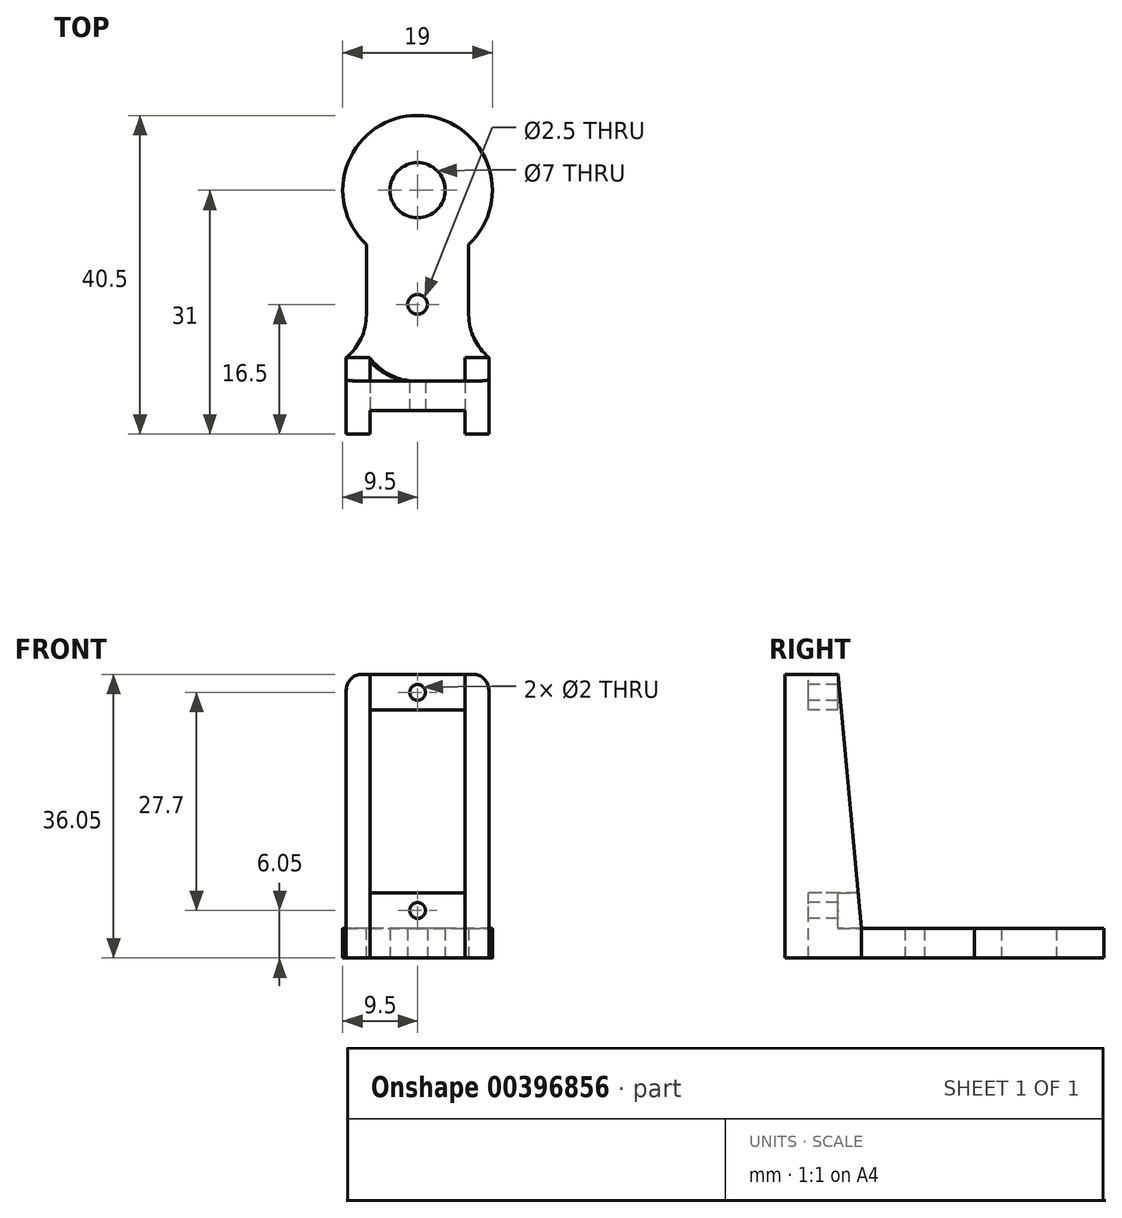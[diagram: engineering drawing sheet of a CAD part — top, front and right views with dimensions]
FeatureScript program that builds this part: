
annotation { "Feature Type Name" : "Feature", "Feature Type Description" : "" }
export const myFeature = defineFeature(function(context is Context, id is Id, definition is map)
    precondition{}
    {
        {
            var Q0;
            Q0=qCreatedBy(makeId("Top.planeOp"),FACE);
            var sketch = newSketch(context, id + "F0", { "sketchPlane" : qUnion([Q0])});
            skCircle(sketch, "E0", {"center": v(0, 0) * mm, "radius": 3.5 * mm});
            skCircle(sketch, "E1", {"center": v(0, 14.5) * mm, "radius": 1.25 * mm});
            skCircle(sketch, "E2", {"center": v(0, 0) * mm, "radius": 6.5 * mm});
            skLineSegment(sketch, "E3.bottom", {"start": v(6.5, 0) * mm, "end": v(-6.5, 0) * mm});
            skLineSegment(sketch, "E3.top", {"start": v(6.5, -28) * mm, "end": v(-6.5, -28) * mm});
            skLineSegment(sketch, "E3.left", {"start": v(6.5, -28) * mm, "end": v(6.5, 0) * mm});
            skLineSegment(sketch, "E3.right", {"start": v(-6.5, -28) * mm, "end": v(-6.5, 0) * mm});
            skCircle(sketch, "E4", {"center": v(0, 14.5) * mm, "radius": 4.25 * mm});
            skLineSegment(sketch, "E5", {"start": v(-6.42, 1) * mm, "end": v(-4.2, 15.16) * mm});
            skLineSegment(sketch, "E6", {"start": v(4.2, 15.16) * mm, "end": v(6.42, 1) * mm});
            skCircle(sketch, "E7", {"center": v(0, -14.5) * mm, "radius": 1.25 * mm});
            skCircle(sketch, "E8", {"center": v(0, 0) * mm, "radius": 9.5 * mm});
            skSolve(sketch);
        }
        {
            var Q0;
            {var subQ1=sQuery(id+"F0.wireOp",EDGE,"E3.top");Q0=makeQuery(id+"F0.imprint","IMPRINT",FACE,{"disambiguationData":[TD([[makeQuery(id+"F0.imprint","IMPRINT",EDGE,{"derivedFrom":subQ1}),-1.0]])]});}
            var Q1;
            {var subQ1=sQuery(id+"F0.wireOp",EDGE,"E2");var subQ3=sQuery(id+"F0.wireOp",EDGE,"E6");var subQ4=makeQuery(id+"F0.imprint","INTERSECT",VERTEX,{"derivedFrom":[subQ1,subQ3]});Q1=makeQuery(id+"F0.imprint","IMPRINT",FACE,{"disambiguationData":[TD([[makeQuery(id+"F0.imprint","IMPRINT",EDGE,{"disambiguationData":[TD([[subQ4,1.0]])],"derivedFrom":subQ3}),1.0]])]});}
            var Q2;
            {var subQ1=sQuery(id+"F0.wireOp",EDGE,"E2");var subQ3=sQuery(id+"F0.wireOp",EDGE,"E5");var subQ4=makeQuery(id+"F0.imprint","INTERSECT",VERTEX,{"derivedFrom":[subQ1,subQ3]});Q2=makeQuery(id+"F0.imprint","IMPRINT",FACE,{"disambiguationData":[TD([[makeQuery(id+"F0.imprint","IMPRINT",EDGE,{"disambiguationData":[TD([[subQ4,-1.0]])],"derivedFrom":subQ3}),1.0]])]});}
            var Q3;
            {var subQ0=sQuery(id+"F0.wireOp",EDGE,"E5");var subQ1=sQuery(id+"F0.wireOp",EDGE,"E2");var subQ2=makeQuery(id+"F0.imprint","INTERSECT",VERTEX,{"derivedFrom":[subQ1,subQ0]});Q3=makeQuery(id+"F0.imprint","IMPRINT",FACE,{"disambiguationData":[TD([[makeQuery(id+"F0.imprint","IMPRINT",EDGE,{"disambiguationData":[TD([[subQ2,1.0]])],"derivedFrom":subQ1}),-1.0]])]});}
            var Q4;
            {var subQ0=sQuery(id+"F0.wireOp",EDGE,"E3.left");var subQ6=sQuery(id+"F0.wireOp",EDGE,"E8");var subQ7=makeQuery(id+"F0.imprint","INTERSECT",VERTEX,{"derivedFrom":[subQ0,subQ6]});Q4=makeQuery(id+"F0.imprint","IMPRINT",FACE,{"disambiguationData":[TD([[makeQuery(id+"F0.imprint","IMPRINT",EDGE,{"disambiguationData":[TD([[subQ7,1.0]])],"derivedFrom":subQ6}),1.0]])]});}
            var Q5;
            {var subQ0=sQuery(id+"F0.wireOp",EDGE,"E3.bottom");var subQ1=sQuery(id+"F0.wireOp",EDGE,"E0");var subQ2=makeQuery(id+"F0.imprint","INTERSECT",VERTEX,{"disambiguationData":[OD(0.0)],"derivedFrom":[subQ1,subQ0]});Q5=makeQuery(id+"F0.imprint","IMPRINT",FACE,{"disambiguationData":[TD([[makeQuery(id+"F0.imprint","IMPRINT",EDGE,{"disambiguationData":[TD([[subQ2,1.0]])],"derivedFrom":subQ1}),-1.0]])]});}
            var Q6;
            {var subQ3=sQuery(id+"F0.wireOp",EDGE,"E3.bottom");var subQ6=sQuery(id+"F0.wireOp",EDGE,"E0");var subQ7=makeQuery(id+"F0.imprint","INTERSECT",VERTEX,{"disambiguationData":[OD(0.0)],"derivedFrom":[subQ6,subQ3]});Q6=makeQuery(id+"F0.imprint","IMPRINT",FACE,{"disambiguationData":[TD([[makeQuery(id+"F0.imprint","IMPRINT",EDGE,{"disambiguationData":[TD([[subQ7,-1.0]])],"derivedFrom":subQ6}),-1.0]])]});}
            extrude(context, id + "F1", {"entities" : qUnion([Q0, Q1, Q2, Q3, Q4, Q5, Q6]), "depth" : 3.75 * mm, "offsetDistance" : 25 * mm});
        }
        {
            var Q0;
            Q0=makeQuery(id+"F1.opExtrude","SWEPT_FACE",FACE,{"disambiguationData":[OSD([sQuery(id+"F0.wireOp",EDGE,"E3.top")])]});
            cPlane(context, id + "F2", {"entities" : qUnion([Q0]), "cplaneType" : CPlaneType.OFFSET, "offset" : 0 * mm, "width" : 150 * mm, "height" : 150 * mm});
        }
        {
            var Q0;
            Q0=qCreatedBy(id+"F2.planeOp",FACE);
            var sketch = newSketch(context, id + "F3", { "sketchPlane" : qUnion([Q0])});
            skLineSegment(sketch, "E9.bottom", {"start": v(-6.05, 31.25) * mm, "end": v(6.05, 31.25) * mm});
            skLineSegment(sketch, "E9.top", {"start": v(-6.05, 8.55) * mm, "end": v(6.05, 8.55) * mm});
            skLineSegment(sketch, "E9.left", {"start": v(-6.05, 31.25) * mm, "end": v(-6.05, 8.55) * mm});
            skLineSegment(sketch, "E9.right", {"start": v(6.05, 31.25) * mm, "end": v(6.05, 8.55) * mm});
            skLineSegment(sketch, "E10.bottom", {"start": v(-9.05, 36.05) * mm, "end": v(9.05, 36.05) * mm});
            skLineSegment(sketch, "E10.top", {"start": v(-9.05, 3.75) * mm, "end": v(9.05, 3.75) * mm});
            skLineSegment(sketch, "E10.left", {"start": v(-9.05, 36.05) * mm, "end": v(-9.05, 3.75) * mm});
            skLineSegment(sketch, "E10.right", {"start": v(9.05, 36.05) * mm, "end": v(9.05, 3.75) * mm});
            skLineSegment(sketch, "E11", {"start": v(-6.05, 19.9) * mm, "end": v(-9.05, 19.9) * mm});
            skPoint(sketch, "E11.startSnap0", {"position": v(-6.05, 19.9) * mm});
            skCircle(sketch, "E12", {"center": v(0, 6.05) * mm, "radius": 1 * mm});
            skPoint(sketch, "E12.centerSnap0", {"position": v(0, 8.55) * mm});
            skCircle(sketch, "E13", {"center": v(0, 33.75) * mm, "radius": 1 * mm});
            skPoint(sketch, "E13.centerSnap0", {"position": v(0, 31.25) * mm});
            skLineSegment(sketch, "E14.bottom", {"start": v(-6.5, 3.75) * mm, "end": v(6.5, 3.75) * mm});
            skLineSegment(sketch, "E14.top", {"start": v(-6.5, 0) * mm, "end": v(6.5, 0) * mm});
            skLineSegment(sketch, "E14.left", {"start": v(-6.5, 3.75) * mm, "end": v(-6.5, 0) * mm});
            skLineSegment(sketch, "E14.right", {"start": v(6.5, 3.75) * mm, "end": v(6.5, 0) * mm});
            skLineSegment(sketch, "E15.top", {"start": v(-6.05, 8.3) * mm, "end": v(6.05, 8.3) * mm});
            skLineSegment(sketch, "E15.left", {"start": v(-6.05, 8.55) * mm, "end": v(-6.05, 8.3) * mm});
            skLineSegment(sketch, "E15.right", {"start": v(6.05, 8.55) * mm, "end": v(6.05, 8.3) * mm});
            skLineSegment(sketch, "E16.top", {"start": v(-6.05, 31.5) * mm, "end": v(6.05, 31.5) * mm});
            skLineSegment(sketch, "E16.left", {"start": v(-6.05, 31.25) * mm, "end": v(-6.05, 31.5) * mm});
            skLineSegment(sketch, "E16.right", {"start": v(6.05, 31.25) * mm, "end": v(6.05, 31.5) * mm});
            skLineSegment(sketch, "E17.top", {"start": v(-9.05, 0) * mm, "end": v(9.05, 0) * mm});
            skLineSegment(sketch, "E17.left", {"start": v(-9.05, 3.75) * mm, "end": v(-9.05, 0) * mm});
            skLineSegment(sketch, "E17.right", {"start": v(9.05, 3.75) * mm, "end": v(9.05, 0) * mm});
            skSolve(sketch);
        }
        {
            var Q0;
            {var subQ8=sQuery(id+"F3.wireOp",EDGE,"E14.right");var subQ11=sQuery(id+"F3.wireOp",EDGE,"E14.left");var subQ19=makeQuery(id+"F3.imprint","IMPRINT",EDGE,{"derivedFrom":subQ8});var subQ21=sQuery(id+"F3.wireOp",EDGE,"E14.top");var subQ22=makeQuery(id+"F3.imprint","IMPRINT",EDGE,{"derivedFrom":subQ11});Q0=qUnion([makeQuery(id+"F3.imprint","IMPRINT",FACE,{"disambiguationData":[TD([[subQ22,-1.0]])]}),makeQuery(id+"F3.imprint","IMPRINT",FACE,{"disambiguationData":[TD([[makeQuery(id+"F3.imprint","IMPRINT",EDGE,{"derivedFrom":subQ21}),1.0]])]}),makeQuery(id+"F3.imprint","IMPRINT",FACE,{"disambiguationData":[TD([[subQ19,1.0]])]}),makeQuery(id+"F3.imprint","IMPRINT",FACE,{"disambiguationData":[TD([[makeQuery(id+"F3.imprint","IMPRINT",EDGE,{"derivedFrom":sQuery(id+"F3.wireOp",EDGE,"E9.right")}),1.0]])]})]);}
            extrude(context, id + "F4", {"entities" : qUnion([Q0]), "operationType" : NewBodyOperationType.ADD, "oppositeDirection" : true, "depth" : 3.75 * mm});
        }
        {
            var Q0;
            Q0=makeQuery(id+"F4.opExtrude","SWEPT_FACE",FACE,{"disambiguationData":[OSD([sQuery(id+"F3.wireOp",EDGE,"E10.right"),sQuery(id+"F3.wireOp",EDGE,"E17.right")])]});
            var sketch = newSketch(context, id + "F5", { "sketchPlane" : qUnion([Q0])});
            skLineSegment(sketch, "E18.bottom", {"start": v(-24.25, 36.05) * mm, "end": v(-31, 36.05) * mm});
            skLineSegment(sketch, "E18.top", {"start": v(-24.25, 0) * mm, "end": v(-31, 0) * mm});
            skLineSegment(sketch, "E18.left", {"start": v(-24.25, 36.05) * mm, "end": v(-24.25, 0) * mm});
            skLineSegment(sketch, "E18.right", {"start": v(-31, 36.05) * mm, "end": v(-31, 0) * mm});
            skLineSegment(sketch, "E19", {"start": v(-24.25, 36.05) * mm, "end": v(-21.25, 3.75) * mm});
            skLineSegment(sketch, "E20", {"start": v(-21.25, 3.75) * mm, "end": v(-21.25, 0) * mm});
            skLineSegment(sketch, "E21", {"start": v(-21.25, 0) * mm, "end": v(-24.25, 0) * mm});
            skSolve(sketch);
        }
        {
            var Q0;
            {var subQ2=sQuery(id+"F5.wireOp",EDGE,"E18.right");Q0=makeQuery(id+"F5.imprint","IMPRINT",FACE,{"disambiguationData":[TD([[makeQuery(id+"F5.imprint","IMPRINT",EDGE,{"derivedFrom":subQ2}),1.0]])]});}
            var Q1;
            Q1=makeQuery(id+"F5.imprint","IMPRINT",FACE,{"disambiguationData":[TD([[makeQuery(id+"F5.imprint","IMPRINT",EDGE,{"derivedFrom":sQuery(id+"F5.wireOp",EDGE,"E18.left")}),1.0]])]});
            var Q2;
            Q2=makeQuery(id+"F4.opExtrude","SWEPT_FACE",FACE,{"disambiguationData":[OSD([sQuery(id+"F3.wireOp",EDGE,"E9.right"),sQuery(id+"F3.wireOp",EDGE,"E15.right"),sQuery(id+"F3.wireOp",EDGE,"E16.right")])]});
            extrude(context, id + "F6", {"entities" : qUnion([Q0, Q1]), "operationType" : NewBodyOperationType.ADD, "endBound" : BoundingType.UP_TO_SURFACE, "oppositeDirection" : true, "depth" : 25 * mm, "endBoundEntityFace" : qUnion([Q2]), "offsetDistance" : 25 * mm});
        }
        {
            var Q0;
            Q0=makeQuery(id+"F4.opExtrude","SWEPT_FACE",FACE,{"disambiguationData":[OSD([sQuery(id+"F3.wireOp",EDGE,"E10.left"),sQuery(id+"F3.wireOp",EDGE,"E17.left")])]});
            var sketch = newSketch(context, id + "F7", { "sketchPlane" : qUnion([Q0])});
            skLineSegment(sketch, "E22", {"start": v(24.25, 36.05) * mm, "end": v(31, 36.05) * mm});
            skLineSegment(sketch, "E23", {"start": v(31, 36.05) * mm, "end": v(31, 0) * mm});
            skLineSegment(sketch, "E24", {"start": v(31, 0) * mm, "end": v(21.25, 0) * mm});
            skLineSegment(sketch, "E25", {"start": v(21.25, 0) * mm, "end": v(21.25, 3.75) * mm});
            skLineSegment(sketch, "E26", {"start": v(21.25, 3.75) * mm, "end": v(24.25, 36.05) * mm});
            skSolve(sketch);
        }
        {
            var Q0;
            {var subQ2=sQuery(id+"F7.wireOp",EDGE,"E23");Q0=makeQuery(id+"F7.imprint","IMPRINT",FACE,{"disambiguationData":[TD([[makeQuery(id+"F7.imprint","IMPRINT",EDGE,{"derivedFrom":subQ2}),-1.0]])]});}
            var Q1;
            {var subQ2=sQuery(id+"F7.wireOp",EDGE,"E25");Q1=makeQuery(id+"F7.imprint","IMPRINT",FACE,{"disambiguationData":[TD([[makeQuery(id+"F7.imprint","IMPRINT",EDGE,{"derivedFrom":subQ2}),-1.0]])]});}
            var Q2;
            Q2=makeQuery(id+"F4.opExtrude","SWEPT_FACE",FACE,{"disambiguationData":[OSD([sQuery(id+"F3.wireOp",EDGE,"E9.left"),sQuery(id+"F3.wireOp",EDGE,"E15.left"),sQuery(id+"F3.wireOp",EDGE,"E16.left")])]});
            extrude(context, id + "F8", {"entities" : qUnion([Q0, Q1]), "operationType" : NewBodyOperationType.ADD, "endBound" : BoundingType.UP_TO_SURFACE, "oppositeDirection" : true, "depth" : 25 * mm, "endBoundEntityFace" : qUnion([Q2]), "offsetDistance" : 25 * mm});
        }
        {
            var Q0;
            Q0=makeQuery(id+"F8.boolean.opBoolean","MERGE",EDGE,{"derivedFrom":[makeQuery(id+"F4.opExtrude","SWEPT_EDGE",EDGE,{"disambiguationData":[OSD([sQuery(id+"F3.wireOp",EDGE,"E10.bottom"),sQuery(id+"F3.wireOp",EDGE,"E10.left")])]}),makeQuery(id+"F8.opExtrude","CAP_EDGE",EDGE,{"disambiguationData":[OSD([sQuery(id+"F7.wireOp",EDGE,"E22")])],"isStart":true})]});
            var Q1;
            Q1=makeQuery(id+"F6.boolean.opBoolean","MERGE",EDGE,{"derivedFrom":[makeQuery(id+"F4.opExtrude","SWEPT_EDGE",EDGE,{"disambiguationData":[OSD([sQuery(id+"F3.wireOp",EDGE,"E10.bottom"),sQuery(id+"F3.wireOp",EDGE,"E10.right")])]}),makeQuery(id+"F6.opExtrude","CAP_EDGE",EDGE,{"disambiguationData":[OSD([sQuery(id+"F5.wireOp",EDGE,"E18.bottom")])],"isStart":true})]});
            var Q2;
            Q2=makeQuery(id+"F6.boolean.opBoolean","MERGE",EDGE,{"derivedFrom":[makeQuery(id+"F4.opExtrude","SWEPT_EDGE",EDGE,{"disambiguationData":[OSD([sQuery(id+"F3.wireOp",EDGE,"E10.bottom"),sQuery(id+"F3.wireOp",EDGE,"E10.right")])]}),makeQuery(id+"F6.opExtrude","CAP_EDGE",EDGE,{"disambiguationData":[OSD([sQuery(id+"F5.wireOp",EDGE,"E18.bottom")])],"isStart":true})]});
            var Q3;
            Q3=makeQuery(id+"F8.boolean.opBoolean","MERGE",EDGE,{"derivedFrom":[makeQuery(id+"F4.opExtrude","SWEPT_EDGE",EDGE,{"disambiguationData":[OSD([sQuery(id+"F3.wireOp",EDGE,"E10.bottom"),sQuery(id+"F3.wireOp",EDGE,"E10.left")])]}),makeQuery(id+"F8.opExtrude","CAP_EDGE",EDGE,{"disambiguationData":[OSD([sQuery(id+"F7.wireOp",EDGE,"E22")])],"isStart":true})]});
            var Q4;
            Q4=makeQuery(id+"F4.boolean.opBoolean","MERGE",EDGE,{"derivedFrom":[makeQuery(id+"F1.opExtrude","CAP_EDGE",EDGE,{"disambiguationData":[OSD([sQuery(id+"F0.wireOp",EDGE,"E3.right")])],"isStart":false}),makeQuery(id+"F4.opExtrude","SWEPT_EDGE",EDGE,{"disambiguationData":[OSD([sQuery(id+"F3.wireOp",EDGE,"E10.top"),sQuery(id+"F3.wireOp",EDGE,"E14.bottom"),sQuery(id+"F3.wireOp",EDGE,"E14.left")])]})]});
            var Q5;
            Q5=makeQuery(id+"F4.boolean.opBoolean","MERGE",EDGE,{"derivedFrom":[makeQuery(id+"F1.opExtrude","CAP_EDGE",EDGE,{"disambiguationData":[OSD([sQuery(id+"F0.wireOp",EDGE,"E3.left")])],"isStart":false}),makeQuery(id+"F4.opExtrude","SWEPT_EDGE",EDGE,{"disambiguationData":[OSD([sQuery(id+"F3.wireOp",EDGE,"E10.top"),sQuery(id+"F3.wireOp",EDGE,"E14.bottom"),sQuery(id+"F3.wireOp",EDGE,"E14.right")])]})]});
            fillet(context, id + "F9", {"entities" : qUnion([Q0, Q1, Q2, Q3, Q4, Q5]), "radius" : 2 * mm, "tangentPropagation" : true, "allowEdgeOverflow" : false});
        }
        {
            var Q0;
            Q0=makeQuery(id+"F4.boolean.opBoolean","INTERSECT",EDGE,{"derivedFrom":[makeQuery(id+"F1.opExtrude","SWEPT_FACE",FACE,{"disambiguationData":[OSD([sQuery(id+"F0.wireOp",EDGE,"E3.left")])]}),makeQuery(id+"F4.opExtrude","CAP_FACE",FACE,{"disambiguationData":[OSD([sQuery(id+"F3.wireOp",EDGE,"E9.left"),sQuery(id+"F3.wireOp",EDGE,"E9.right"),sQuery(id+"F3.wireOp",EDGE,"E10.bottom"),sQuery(id+"F3.wireOp",EDGE,"E10.left"),sQuery(id+"F3.wireOp",EDGE,"E10.right"),sQuery(id+"F3.wireOp",EDGE,"E12"),sQuery(id+"F3.wireOp",EDGE,"E13"),sQuery(id+"F3.wireOp",EDGE,"E9.top"),sQuery(id+"F3.wireOp",EDGE,"E15.top"),sQuery(id+"F3.wireOp",EDGE,"E15.left"),sQuery(id+"F3.wireOp",EDGE,"E15.right"),sQuery(id+"F3.wireOp",EDGE,"E16.top"),sQuery(id+"F3.wireOp",EDGE,"E16.left"),sQuery(id+"F3.wireOp",EDGE,"E16.right"),sQuery(id+"F3.wireOp",EDGE,"E17.top"),sQuery(id+"F3.wireOp",EDGE,"E17.left"),sQuery(id+"F3.wireOp",EDGE,"E17.right")])],"isStart":false})]});
            var Q1;
            Q1=makeQuery(id+"F4.boolean.opBoolean","INTERSECT",EDGE,{"derivedFrom":[makeQuery(id+"F1.opExtrude","SWEPT_FACE",FACE,{"disambiguationData":[OSD([sQuery(id+"F0.wireOp",EDGE,"E3.right")])]}),makeQuery(id+"F4.opExtrude","CAP_FACE",FACE,{"disambiguationData":[OSD([sQuery(id+"F3.wireOp",EDGE,"E9.left"),sQuery(id+"F3.wireOp",EDGE,"E9.right"),sQuery(id+"F3.wireOp",EDGE,"E10.bottom"),sQuery(id+"F3.wireOp",EDGE,"E10.left"),sQuery(id+"F3.wireOp",EDGE,"E10.right"),sQuery(id+"F3.wireOp",EDGE,"E12"),sQuery(id+"F3.wireOp",EDGE,"E13"),sQuery(id+"F3.wireOp",EDGE,"E9.top"),sQuery(id+"F3.wireOp",EDGE,"E15.top"),sQuery(id+"F3.wireOp",EDGE,"E15.left"),sQuery(id+"F3.wireOp",EDGE,"E15.right"),sQuery(id+"F3.wireOp",EDGE,"E16.top"),sQuery(id+"F3.wireOp",EDGE,"E16.left"),sQuery(id+"F3.wireOp",EDGE,"E16.right"),sQuery(id+"F3.wireOp",EDGE,"E17.top"),sQuery(id+"F3.wireOp",EDGE,"E17.left"),sQuery(id+"F3.wireOp",EDGE,"E17.right")])],"isStart":false})]});
            var Q2;
            {var subQ0=sQuery(id+"F3.wireOp",EDGE,"E15.top");var subQ6=sQuery(id+"F5.wireOp",EDGE,"E18.left");Q2=makeQuery(id+"F6.boolean.opBoolean","SPLIT",EDGE,{"disambiguationData":[TD([makeQuery(id+"F4.opExtrude","SWEPT_FACE",FACE,{"disambiguationData":[OSD([subQ0])]})])],"derivedFrom":makeQuery(id+"F6.opExtrude","CAP_EDGE",EDGE,{"disambiguationData":[OSD([subQ6])],"isStart":false})});}
            var Q3;
            {var subQ0=sQuery(id+"F3.wireOp",EDGE,"E15.top");var subQ4=sQuery(id+"F3.wireOp",EDGE,"E17.left");var subQ5=sQuery(id+"F3.wireOp",EDGE,"E10.left");Q3=makeQuery(id+"F8.boolean.opBoolean","SPLIT",EDGE,{"disambiguationData":[TD([makeQuery(id+"F4.opExtrude","SWEPT_FACE",FACE,{"disambiguationData":[OSD([subQ0])]})])],"derivedFrom":makeQuery(id+"F8.opExtrude","CAP_EDGE",EDGE,{"disambiguationData":[OSD([subQ5,subQ4]),TDD([makeQuery(id+"F7.imprint","IMPRINT",EDGE,{"derivedFrom":makeQuery(id+"F4.opExtrude","CAP_EDGE",EDGE,{"disambiguationData":[OSD([subQ5,subQ4])],"isStart":false})})])],"isStart":false})});}
            var Q4;
            Q4=makeQuery(id+"F6.boolean.opBoolean","INTERSECT",EDGE,{"derivedFrom":[makeQuery(id+"F1.opExtrude","SWEPT_FACE",FACE,{"disambiguationData":[OSD([sQuery(id+"F0.wireOp",EDGE,"E3.left")])]}),makeQuery(id+"F6.opExtrude","SWEPT_FACE",FACE,{"disambiguationData":[OSD([sQuery(id+"F5.wireOp",EDGE,"E20")])]})]});
            var Q5;
            Q5=makeQuery(id+"F8.boolean.opBoolean","INTERSECT",EDGE,{"derivedFrom":[makeQuery(id+"F1.opExtrude","SWEPT_FACE",FACE,{"disambiguationData":[OSD([sQuery(id+"F0.wireOp",EDGE,"E3.right")])]}),makeQuery(id+"F8.opExtrude","SWEPT_FACE",FACE,{"disambiguationData":[OSD([sQuery(id+"F7.wireOp",EDGE,"E25")])]})]});
            fillet(context, id + "F10", {"entities" : qUnion([Q0, Q1, Q2, Q3, Q4, Q5]), "radius" : 7 * mm, "tangentPropagation" : true, "allowEdgeOverflow" : false});
        }
    });
